# Revit family: Drop Leaf Table HM6
name_source: partatom
category: Furniture
revit_build: Autodesk Revit 2017 (Build: 20171027_0315(x64)
units: mm (PartAtom-declared; Revit-internal decimal feet)

## family parameters
Always vertical = Yes
Cut with Voids When Loaded = No
OmniClass Number = 23.40.20.00
OmniClass Title = General Furniture and Specialties
Room Calculation Point = No
Shared = No
Work Plane-Based = No

## types (1)
- Drop Leaf Table HM6
    Depth = 163cm / 64.2in
    Description = Looking to create a versatile piece that would adapt to its surroundings, design duo Hvidt & Mølgaard devised this handsome lounge table. As part of the Drop Leaf series, it boasts the same curved wooden frames and easily foldable design. Available in solid walnut or oak.
    Design = Hvidt & Mølgaard
    Design Year = 1956
    Fittings = &tradition Polished Brass
    Frame horizontal = &tradition Walnut Oiled Horizontal
    Frame vertical = &tradition Walnut Oiled Vertical
    Gliders = &tradition Plastic Black Matt
    Height = 73cm / 28.7in
    Manufacturer = &tradition
    Model = Drop Leaf Table HM6
    Packaging Dimensions = H: 73cm/28.7in, W: 142cm/55.9in, D: 163cm/64.2in
    Table Top = &tradition Walnut Oiled Vertical
    Table Top Support = &tradition Polished Brass
    Type Comments = Drop Leaf Series
    URL = https://www.andtradition.com
    Variations = Available in Oiled Oak
    Weight = 41 kg
    Width = 142cm / 55.9in

## geometry (parser evidence)
native form markers: Sweep x2
no freeform markers — native parametric forms only
